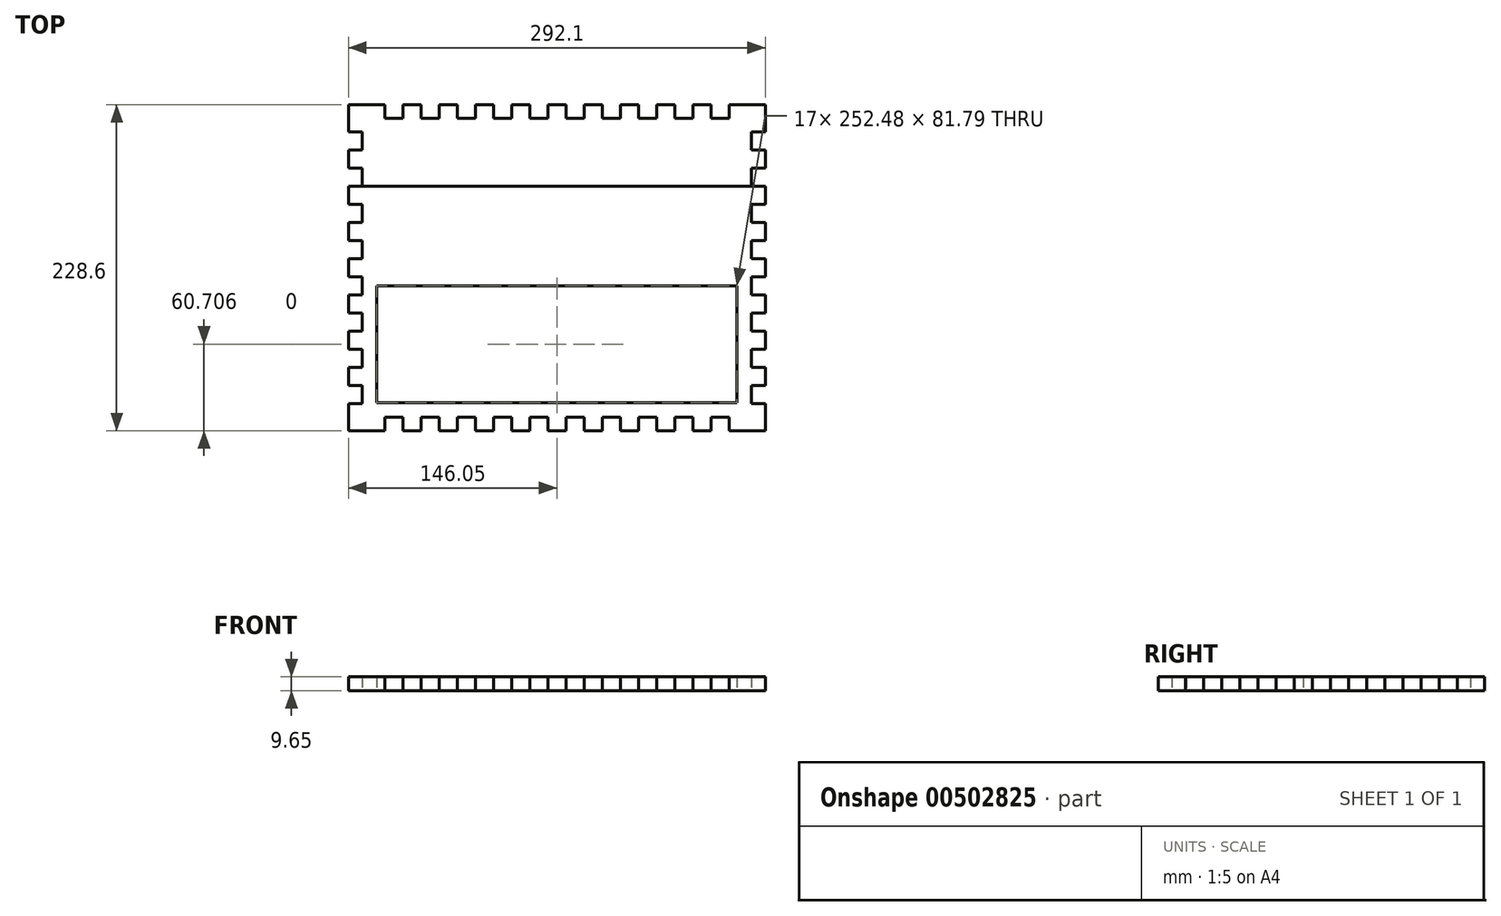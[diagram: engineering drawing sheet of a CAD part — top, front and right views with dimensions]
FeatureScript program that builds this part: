
annotation { "Feature Type Name" : "Feature", "Feature Type Description" : "" }
export const myFeature = defineFeature(function(context is Context, id is Id, definition is map)
    precondition{}
    {
        {
            var Q0;
            Q0=qCreatedBy(makeId("Top.planeOp"),FACE);
            var sketch = newSketch(context, id + "F0", { "sketchPlane" : qUnion([Q0])});
            skLineSegment(sketch, "E0.bottom", {"start": v(0, 0) * mm, "end": v(25.4, 0) * mm});
            skLineSegment(sketch, "E0.left", {"start": v(0, 0) * mm, "end": v(0, -19.05) * mm});
            skLineSegment(sketch, "E1", {"start": v(25.4, 0) * mm, "end": v(25.4, -9.65) * mm});
            skLineSegment(sketch, "E2", {"start": v(25.4, -9.65) * mm, "end": v(38.1, -9.65) * mm});
            skLineSegment(sketch, "E3", {"start": v(38.1, -9.65) * mm, "end": v(38.1, 0) * mm});
            skLineSegment(sketch, "E4", {"start": v(38.1, 0) * mm, "end": v(50.8, 0) * mm});
            skLineSegment(sketch, "E5", {"start": v(50.8, 0) * mm, "end": v(50.8, -9.65) * mm});
            skLineSegment(sketch, "E6", {"start": v(50.8, -9.65) * mm, "end": v(63.5, -9.65) * mm});
            skLineSegment(sketch, "E7", {"start": v(63.5, -9.65) * mm, "end": v(63.5, 0) * mm});
            skLineSegment(sketch, "E8.trimOffspring", {"start": v(63.5, 0) * mm, "end": v(76.2, 0) * mm});
            skLineSegment(sketch, "E9", {"start": v(76.2, 0) * mm, "end": v(76.2, -9.65) * mm});
            skLineSegment(sketch, "E10", {"start": v(76.2, -9.65) * mm, "end": v(88.9, -9.65) * mm});
            skLineSegment(sketch, "E11", {"start": v(88.9, -9.65) * mm, "end": v(88.9, 0) * mm});
            skLineSegment(sketch, "E12", {"start": v(88.9, 0) * mm, "end": v(101.6, 0) * mm});
            skLineSegment(sketch, "E13", {"start": v(101.6, 0) * mm, "end": v(101.6, -9.65) * mm});
            skLineSegment(sketch, "E14", {"start": v(101.6, -9.65) * mm, "end": v(114.3, -9.65) * mm});
            skLineSegment(sketch, "E15", {"start": v(114.3, -9.65) * mm, "end": v(114.3, 0) * mm});
            skLineSegment(sketch, "E16", {"start": v(114.3, 0) * mm, "end": v(127, 0) * mm});
            skLineSegment(sketch, "E17", {"start": v(127, 0) * mm, "end": v(127, -9.65) * mm});
            skLineSegment(sketch, "E18", {"start": v(127, -9.65) * mm, "end": v(139.7, -9.65) * mm});
            skLineSegment(sketch, "E19", {"start": v(139.7, -9.65) * mm, "end": v(139.7, 0) * mm});
            skLineSegment(sketch, "E20.trimOffspring", {"start": v(139.7, 0) * mm, "end": v(152.4, 0) * mm});
            skLineSegment(sketch, "E21", {"start": v(152.4, 0) * mm, "end": v(152.4, -9.65) * mm});
            skLineSegment(sketch, "E22", {"start": v(152.4, -9.65) * mm, "end": v(165.1, -9.65) * mm});
            skLineSegment(sketch, "E23", {"start": v(165.1, -9.65) * mm, "end": v(165.1, 0) * mm});
            skLineSegment(sketch, "E24", {"start": v(165.1, 0) * mm, "end": v(177.8, 0) * mm});
            skLineSegment(sketch, "E25", {"start": v(177.8, 0) * mm, "end": v(177.8, -9.65) * mm});
            skLineSegment(sketch, "E26", {"start": v(177.8, -9.65) * mm, "end": v(190.5, -9.65) * mm});
            skLineSegment(sketch, "E27", {"start": v(190.5, -9.65) * mm, "end": v(190.5, 0) * mm});
            skLineSegment(sketch, "E28", {"start": v(190.5, 0) * mm, "end": v(203.2, 0) * mm});
            skLineSegment(sketch, "E29", {"start": v(203.2, 0) * mm, "end": v(203.2, -9.65) * mm});
            skLineSegment(sketch, "E30", {"start": v(203.2, -9.65) * mm, "end": v(215.9, -9.65) * mm});
            skLineSegment(sketch, "E31", {"start": v(215.9, -9.65) * mm, "end": v(215.9, 0) * mm});
            skLineSegment(sketch, "E32.trimOffspring", {"start": v(215.9, 0) * mm, "end": v(228.6, 0) * mm});
            skLineSegment(sketch, "E33", {"start": v(228.6, 0) * mm, "end": v(228.6, -9.65) * mm});
            skLineSegment(sketch, "E34", {"start": v(228.6, -9.65) * mm, "end": v(241.3, -9.65) * mm});
            skLineSegment(sketch, "E35", {"start": v(241.3, -9.65) * mm, "end": v(241.3, 0) * mm});
            skLineSegment(sketch, "E36", {"start": v(241.3, 0) * mm, "end": v(254, 0) * mm});
            skLineSegment(sketch, "E37", {"start": v(254, 0) * mm, "end": v(254, -9.65) * mm});
            skLineSegment(sketch, "E38", {"start": v(254, -9.65) * mm, "end": v(266.7, -9.65) * mm});
            skLineSegment(sketch, "E39", {"start": v(266.7, -9.65) * mm, "end": v(266.7, 0) * mm});
            skLineSegment(sketch, "E40.trimOffspring", {"start": v(266.7, 0) * mm, "end": v(292.1, 0) * mm});
            skLineSegment(sketch, "E41", {"start": v(0, -19.05) * mm, "end": v(9.65, -19.05) * mm});
            skLineSegment(sketch, "E42", {"start": v(9.65, -19.05) * mm, "end": v(9.65, -31.75) * mm});
            skLineSegment(sketch, "E43", {"start": v(9.65, -31.75) * mm, "end": v(0, -31.75) * mm});
            skLineSegment(sketch, "E44", {"start": v(0, -31.75) * mm, "end": v(0, -44.45) * mm});
            skLineSegment(sketch, "E45", {"start": v(0, -44.45) * mm, "end": v(9.65, -44.45) * mm});
            skLineSegment(sketch, "E46", {"start": v(9.65, -44.45) * mm, "end": v(9.65, -57.15) * mm});
            skLineSegment(sketch, "E47", {"start": v(9.65, -57.15) * mm, "end": v(0, -57.15) * mm});
            skLineSegment(sketch, "E48.trimOffspring", {"start": v(0, -57.15) * mm, "end": v(0, -69.85) * mm});
            skLineSegment(sketch, "E49", {"start": v(0, -69.85) * mm, "end": v(9.65, -69.85) * mm});
            skLineSegment(sketch, "E50", {"start": v(9.65, -69.85) * mm, "end": v(9.65, -82.55) * mm});
            skLineSegment(sketch, "E51", {"start": v(9.65, -82.55) * mm, "end": v(0, -82.55) * mm});
            skLineSegment(sketch, "E52", {"start": v(0, -82.55) * mm, "end": v(0, -95.25) * mm});
            skLineSegment(sketch, "E53", {"start": v(0, -95.25) * mm, "end": v(9.65, -95.25) * mm});
            skLineSegment(sketch, "E54", {"start": v(9.65, -95.25) * mm, "end": v(9.65, -107.95) * mm});
            skLineSegment(sketch, "E55", {"start": v(9.65, -107.95) * mm, "end": v(0, -107.95) * mm});
            skLineSegment(sketch, "E56", {"start": v(0, -107.95) * mm, "end": v(0, -120.65) * mm});
            skLineSegment(sketch, "E57", {"start": v(0, -120.65) * mm, "end": v(9.65, -120.65) * mm});
            skLineSegment(sketch, "E58", {"start": v(9.65, -120.65) * mm, "end": v(9.65, -133.35) * mm});
            skLineSegment(sketch, "E59", {"start": v(9.65, -133.35) * mm, "end": v(0, -133.35) * mm});
            skLineSegment(sketch, "E60.trimOffspring", {"start": v(0, -133.35) * mm, "end": v(0, -146.05) * mm});
            skLineSegment(sketch, "E61", {"start": v(0, -146.05) * mm, "end": v(9.65, -146.05) * mm});
            skLineSegment(sketch, "E62", {"start": v(9.65, -146.05) * mm, "end": v(9.65, -158.75) * mm});
            skLineSegment(sketch, "E63", {"start": v(9.65, -158.75) * mm, "end": v(0, -158.75) * mm});
            skLineSegment(sketch, "E64", {"start": v(0, -158.75) * mm, "end": v(0, -171.45) * mm});
            skLineSegment(sketch, "E65", {"start": v(0, -171.45) * mm, "end": v(9.65, -171.45) * mm});
            skLineSegment(sketch, "E66", {"start": v(9.65, -171.45) * mm, "end": v(9.65, -184.15) * mm});
            skLineSegment(sketch, "E67", {"start": v(9.65, -184.15) * mm, "end": v(0, -184.15) * mm});
            skLineSegment(sketch, "E68", {"start": v(0, -184.15) * mm, "end": v(0, -196.85) * mm});
            skLineSegment(sketch, "E69", {"start": v(0, -196.85) * mm, "end": v(9.65, -196.85) * mm});
            skLineSegment(sketch, "E70", {"start": v(9.65, -196.85) * mm, "end": v(9.65, -209.55) * mm});
            skLineSegment(sketch, "E71", {"start": v(9.65, -209.55) * mm, "end": v(0, -209.55) * mm});
            skLineSegment(sketch, "E72.trimOffspring", {"start": v(0, -209.55) * mm, "end": v(0, -228.6) * mm});
            skLineSegment(sketch, "E73", {"start": v(0, -114.3) * mm, "end": v(122.75, -114.3) * mm, "construction": true});
            skLineSegment(sketch, "E74.MirrorCS", {"start": v(0, -228.6) * mm, "end": v(25.4, -228.6) * mm});
            skLineSegment(sketch, "E75.MirrorCS", {"start": v(25.4, -228.6) * mm, "end": v(25.4, -218.95) * mm});
            skLineSegment(sketch, "E76.MirrorCS", {"start": v(25.4, -218.95) * mm, "end": v(38.1, -218.95) * mm});
            skLineSegment(sketch, "E77.MirrorCS", {"start": v(38.1, -218.95) * mm, "end": v(38.1, -228.6) * mm});
            skLineSegment(sketch, "E78.MirrorCS", {"start": v(38.1, -228.6) * mm, "end": v(50.8, -228.6) * mm});
            skLineSegment(sketch, "E79.MirrorCS", {"start": v(50.8, -228.6) * mm, "end": v(50.8, -218.95) * mm});
            skLineSegment(sketch, "E80.MirrorCS", {"start": v(50.8, -218.95) * mm, "end": v(63.5, -218.95) * mm});
            skLineSegment(sketch, "E81.MirrorCS", {"start": v(63.5, -218.95) * mm, "end": v(63.5, -228.6) * mm});
            skLineSegment(sketch, "E82.MirrorCS", {"start": v(63.5, -228.6) * mm, "end": v(76.2, -228.6) * mm});
            skLineSegment(sketch, "E83.MirrorCS", {"start": v(76.2, -228.6) * mm, "end": v(76.2, -218.95) * mm});
            skLineSegment(sketch, "E84.MirrorCS", {"start": v(76.2, -218.95) * mm, "end": v(88.9, -218.95) * mm});
            skLineSegment(sketch, "E85.MirrorCS", {"start": v(88.9, -218.95) * mm, "end": v(88.9, -228.6) * mm});
            skLineSegment(sketch, "E86.MirrorCS", {"start": v(88.9, -228.6) * mm, "end": v(101.6, -228.6) * mm});
            skLineSegment(sketch, "E87.MirrorCS", {"start": v(101.6, -228.6) * mm, "end": v(101.6, -218.95) * mm});
            skLineSegment(sketch, "E88.MirrorCS", {"start": v(101.6, -218.95) * mm, "end": v(114.3, -218.95) * mm});
            skLineSegment(sketch, "E89.MirrorCS", {"start": v(114.3, -218.95) * mm, "end": v(114.3, -228.6) * mm});
            skLineSegment(sketch, "E90.MirrorCS", {"start": v(114.3, -228.6) * mm, "end": v(127, -228.6) * mm});
            skLineSegment(sketch, "E91.MirrorCS", {"start": v(127, -228.6) * mm, "end": v(127, -218.95) * mm});
            skLineSegment(sketch, "E92.MirrorCS", {"start": v(127, -218.95) * mm, "end": v(139.7, -218.95) * mm});
            skLineSegment(sketch, "E93.MirrorCS", {"start": v(139.7, -218.95) * mm, "end": v(139.7, -228.6) * mm});
            skLineSegment(sketch, "E94.MirrorCS", {"start": v(139.7, -228.6) * mm, "end": v(152.4, -228.6) * mm});
            skLineSegment(sketch, "E95.MirrorCS", {"start": v(152.4, -228.6) * mm, "end": v(152.4, -218.95) * mm});
            skLineSegment(sketch, "E96.MirrorCS", {"start": v(152.4, -218.95) * mm, "end": v(165.1, -218.95) * mm});
            skLineSegment(sketch, "E97.MirrorCS", {"start": v(165.1, -218.95) * mm, "end": v(165.1, -228.6) * mm});
            skLineSegment(sketch, "E98.MirrorCS", {"start": v(165.1, -228.6) * mm, "end": v(177.8, -228.6) * mm});
            skLineSegment(sketch, "E99.MirrorCS", {"start": v(177.8, -228.6) * mm, "end": v(177.8, -218.95) * mm});
            skLineSegment(sketch, "E100.MirrorCS", {"start": v(177.8, -218.95) * mm, "end": v(190.5, -218.95) * mm});
            skLineSegment(sketch, "E101.MirrorCS", {"start": v(190.5, -218.95) * mm, "end": v(190.5, -228.6) * mm});
            skLineSegment(sketch, "E102.MirrorCS", {"start": v(190.5, -228.6) * mm, "end": v(203.2, -228.6) * mm});
            skLineSegment(sketch, "E103.MirrorCS", {"start": v(203.2, -228.6) * mm, "end": v(203.2, -218.95) * mm});
            skLineSegment(sketch, "E104.MirrorCS", {"start": v(203.2, -218.95) * mm, "end": v(215.9, -218.95) * mm});
            skLineSegment(sketch, "E105.MirrorCS", {"start": v(215.9, -218.95) * mm, "end": v(215.9, -228.6) * mm});
            skLineSegment(sketch, "E106.MirrorCS", {"start": v(215.9, -228.6) * mm, "end": v(228.6, -228.6) * mm});
            skLineSegment(sketch, "E107.MirrorCS", {"start": v(228.6, -228.6) * mm, "end": v(228.6, -218.95) * mm});
            skLineSegment(sketch, "E108.MirrorCS", {"start": v(228.6, -218.95) * mm, "end": v(241.3, -218.95) * mm});
            skLineSegment(sketch, "E109.MirrorCS", {"start": v(241.3, -218.95) * mm, "end": v(241.3, -228.6) * mm});
            skLineSegment(sketch, "E110.MirrorCS", {"start": v(241.3, -228.6) * mm, "end": v(254, -228.6) * mm});
            skLineSegment(sketch, "E111.MirrorCS", {"start": v(254, -228.6) * mm, "end": v(254, -218.95) * mm});
            skLineSegment(sketch, "E112.MirrorCS", {"start": v(254, -218.95) * mm, "end": v(266.7, -218.95) * mm});
            skLineSegment(sketch, "E113.MirrorCS", {"start": v(266.7, -218.95) * mm, "end": v(266.7, -228.6) * mm});
            skLineSegment(sketch, "E114.MirrorCS", {"start": v(266.7, -228.6) * mm, "end": v(292.1, -228.6) * mm});
            skLineSegment(sketch, "E115", {"start": v(146.05, 0) * mm, "end": v(146.05, -45.27) * mm, "construction": true});
            skLineSegment(sketch, "E116.MirrorCS", {"start": v(292.1, 0) * mm, "end": v(292.1, -19.05) * mm});
            skLineSegment(sketch, "E117.MirrorCS", {"start": v(292.1, -19.05) * mm, "end": v(282.45, -19.05) * mm});
            skLineSegment(sketch, "E118.MirrorCS", {"start": v(282.45, -19.05) * mm, "end": v(282.45, -31.75) * mm});
            skLineSegment(sketch, "E119.MirrorCS", {"start": v(282.45, -31.75) * mm, "end": v(292.1, -31.75) * mm});
            skLineSegment(sketch, "E120.MirrorCS", {"start": v(292.1, -31.75) * mm, "end": v(292.1, -44.45) * mm});
            skLineSegment(sketch, "E121.MirrorCS", {"start": v(292.1, -44.45) * mm, "end": v(282.45, -44.45) * mm});
            skLineSegment(sketch, "E122.MirrorCS", {"start": v(282.45, -44.45) * mm, "end": v(282.45, -57.15) * mm});
            skLineSegment(sketch, "E123.MirrorCS", {"start": v(282.45, -57.15) * mm, "end": v(292.1, -57.15) * mm});
            skLineSegment(sketch, "E124.MirrorCS", {"start": v(292.1, -57.15) * mm, "end": v(292.1, -69.85) * mm});
            skLineSegment(sketch, "E125.MirrorCS", {"start": v(292.1, -69.85) * mm, "end": v(282.45, -69.85) * mm});
            skLineSegment(sketch, "E126.MirrorCS", {"start": v(282.45, -69.85) * mm, "end": v(282.45, -82.55) * mm});
            skLineSegment(sketch, "E127.MirrorCS", {"start": v(282.45, -82.55) * mm, "end": v(292.1, -82.55) * mm});
            skLineSegment(sketch, "E128.MirrorCS", {"start": v(292.1, -82.55) * mm, "end": v(292.1, -95.25) * mm});
            skLineSegment(sketch, "E129.MirrorCS", {"start": v(292.1, -95.25) * mm, "end": v(282.45, -95.25) * mm});
            skLineSegment(sketch, "E130.MirrorCS", {"start": v(282.45, -95.25) * mm, "end": v(282.45, -107.95) * mm});
            skLineSegment(sketch, "E131.MirrorCS", {"start": v(282.45, -107.95) * mm, "end": v(292.1, -107.95) * mm});
            skLineSegment(sketch, "E132.MirrorCS", {"start": v(292.1, -107.95) * mm, "end": v(292.1, -120.65) * mm});
            skLineSegment(sketch, "E133.MirrorCS", {"start": v(292.1, -120.65) * mm, "end": v(282.45, -120.65) * mm});
            skLineSegment(sketch, "E134.MirrorCS", {"start": v(282.45, -120.65) * mm, "end": v(282.45, -133.35) * mm});
            skLineSegment(sketch, "E135.MirrorCS", {"start": v(282.45, -133.35) * mm, "end": v(292.1, -133.35) * mm});
            skLineSegment(sketch, "E136.MirrorCS", {"start": v(292.1, -133.35) * mm, "end": v(292.1, -146.05) * mm});
            skLineSegment(sketch, "E137.MirrorCS", {"start": v(292.1, -146.05) * mm, "end": v(282.45, -146.05) * mm});
            skLineSegment(sketch, "E138.MirrorCS", {"start": v(282.45, -146.05) * mm, "end": v(282.45, -158.75) * mm});
            skLineSegment(sketch, "E139.MirrorCS", {"start": v(282.45, -158.75) * mm, "end": v(292.1, -158.75) * mm});
            skLineSegment(sketch, "E140.MirrorCS", {"start": v(292.1, -158.75) * mm, "end": v(292.1, -171.45) * mm});
            skLineSegment(sketch, "E141.MirrorCS", {"start": v(292.1, -171.45) * mm, "end": v(282.45, -171.45) * mm});
            skLineSegment(sketch, "E142.MirrorCS", {"start": v(282.45, -171.45) * mm, "end": v(282.45, -184.15) * mm});
            skLineSegment(sketch, "E143.MirrorCS", {"start": v(282.45, -184.15) * mm, "end": v(292.1, -184.15) * mm});
            skLineSegment(sketch, "E144.MirrorCS", {"start": v(292.1, -184.15) * mm, "end": v(292.1, -196.85) * mm});
            skLineSegment(sketch, "E145.MirrorCS", {"start": v(292.1, -196.85) * mm, "end": v(282.45, -196.85) * mm});
            skLineSegment(sketch, "E146.MirrorCS", {"start": v(282.45, -196.85) * mm, "end": v(282.45, -209.55) * mm});
            skLineSegment(sketch, "E147.MirrorCS", {"start": v(282.45, -209.55) * mm, "end": v(292.1, -209.55) * mm});
            skLineSegment(sketch, "E148.MirrorCS", {"start": v(292.1, -209.55) * mm, "end": v(292.1, -228.6) * mm});
            skPoint(sketch, "E149.firstSnap0", {"position": v(9.65, -127) * mm});
            skLineSegment(sketch, "E149.bottom", {"start": v(19.81, -127) * mm, "end": v(272.29, -127) * mm});
            skLineSegment(sketch, "E149.top", {"start": v(19.81, -208.79) * mm, "end": v(272.29, -208.79) * mm});
            skLineSegment(sketch, "E149.left", {"start": v(19.81, -127) * mm, "end": v(19.81, -208.79) * mm});
            skLineSegment(sketch, "E149.right", {"start": v(272.29, -127) * mm, "end": v(272.29, -208.79) * mm});
            skLineSegment(sketch, "E150", {"start": v(9.65, -57.15) * mm, "end": v(282.45, -57.15) * mm});
            skSolve(sketch);
        }
        {
            var Q0;
            Q0=makeQuery(id+"F0.imprint","IMPRINT",FACE,{"disambiguationData":[TD([[makeQuery(id+"F0.imprint","IMPRINT",EDGE,{"derivedFrom":sQuery(id+"F0.wireOp",EDGE,"E47")}),1.0]])]});
            extrude(context, id + "F1", {"entities" : qUnion([Q0]), "depth" : 9.65 * mm});
        }
        {
            var Q0;
            Q0=makeQuery(id+"F0.imprint","IMPRINT",FACE,{"disambiguationData":[TD([[makeQuery(id+"F0.imprint","IMPRINT",EDGE,{"derivedFrom":sQuery(id+"F0.wireOp",EDGE,"E0.bottom")}),-1.0]])]});
            extrude(context, id + "F2", {"entities" : qUnion([Q0]), "depth" : 9.65 * mm});
        }
    });
